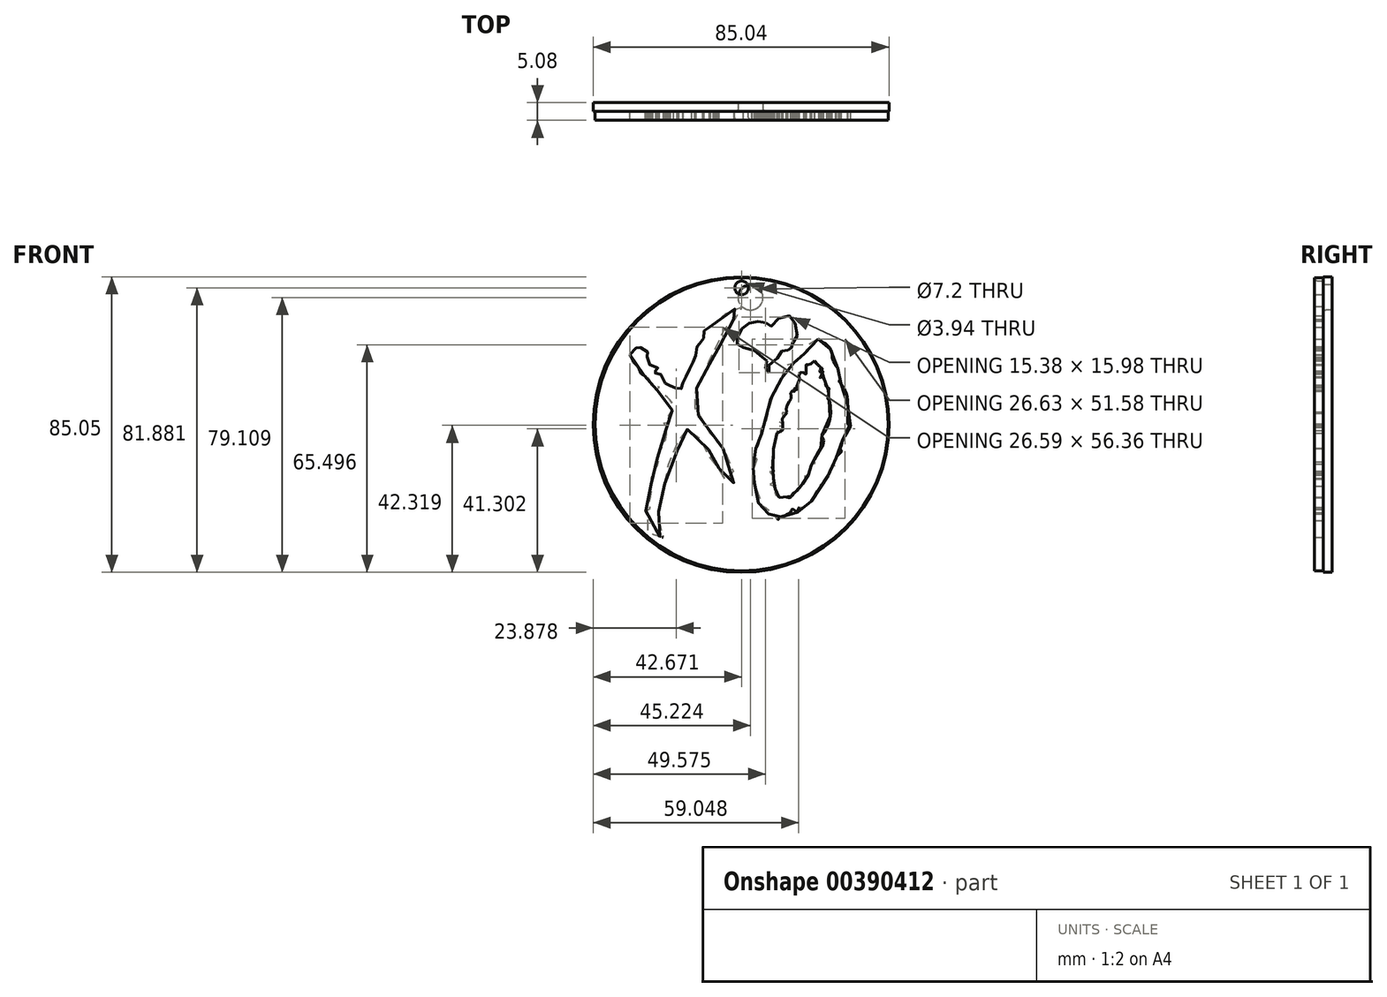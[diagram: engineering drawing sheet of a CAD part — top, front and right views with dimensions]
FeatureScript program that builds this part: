
annotation { "Feature Type Name" : "Feature", "Feature Type Description" : "" }
export const myFeature = defineFeature(function(context is Context, id is Id, definition is map)
    precondition{}
    {
        {
            var Q0;
            Q0=qCreatedBy(makeId("Front.planeOp"),FACE);
            var sketch = newSketch(context, id + "F0", { "sketchPlane" : qUnion([Q0])});
            skFitSpline(sketch, "E0", {"points": [v(-32.07, 22.35) * mm, v(-30.03, 24.5) * mm, v(-29.2, 24.47) * mm, v(-26.86, 22.8) * mm, v(-27.16, 21.56) * mm, v(-25.57, 18.73) * mm, v(-23.72, 18.35) * mm, v(-25.5, 17.07) * mm, v(-23.46, 16.95) * mm, v(-23.16, 16.39) * mm, v(-21, 13.14) * mm, v(-20.44, 13.6) * mm, v(-17.68, 12.08) * mm, v(-17.23, 13.4) * mm, v(-16.47, 14.84) * mm, v(-15.34, 17.37) * mm, v(-14.1, 19.94) * mm, v(-13.11, 22.28) * mm, v(-12.66, 25.26) * mm, v(-12.28, 25.49) * mm, v(-10.96, 26.85) * mm, v(-10.7, 29.22) * mm, v(-9.26, 30.17) * mm], "startDerivative": vector(41.67, 50.3) * mm, "endDerivative": vector(43.04, 15.46) * mm});
            skPoint(sketch, "E1.6.internal.orphan", {"position": v(0, 36.12) * mm});
            skPoint(sketch, "E1.9.internal.orphan", {"position": v(0, 34.47) * mm});
            skFitSpline(sketch, "E2", {"points": [v(-9.26, 30.17) * mm, v(-6.77, 32.25) * mm, v(-5.19, 33.64) * mm, v(-3.26, 34.93) * mm, v(-1.52, 35.68) * mm, v(0, 36.12) * mm, v(0.48, 34.44) * mm, v(0, 34.06) * mm, v(-1.49, 32.55) * mm, v(-2.66, 32.4) * mm, v(-2.92, 31.04) * mm, v(-4.35, 30.17) * mm, v(-6.05, 27) * mm, v(-6.62, 24.32) * mm, v(-7.6, 24.32) * mm, v(-7.19, 23.15) * mm, v(-8.5, 22.54) * mm, v(-9.26, 19.94) * mm, v(-9.87, 17.86) * mm, v(-11.04, 17.1) * mm, v(-11.04, 15.57) * mm, v(-12.24, 13.35) * mm, v(-13.4, 11.72) * mm, v(-13.13, 10.44) * mm, v(-14.17, 9.99) * mm, v(-13.37, 6.87) * mm, v(-11, 2.31) * mm, v(-8.06, -1.39) * mm, v(-5.72, -4.26) * mm, v(-4.51, -6.1) * mm, v(-3.11, -8.68) * mm, v(-2.36, -11.32) * mm, v(-2.62, -15.43) * mm, v(-4.51, -13.85) * mm, v(-5.04, -12.94) * mm, v(-6.78, -11.24) * mm, v(-6.4, -10.49) * mm, v(-7.98, -9.28) * mm, v(-8.1, -7.5) * mm, v(-9.26, -7.17) * mm, v(-8.85, -6.49) * mm, v(-9.9, -4.3) * mm, v(-11.91, -1.88) * mm, v(-14.06, 0.39) * mm, v(-15.16, 1.33) * mm, v(-16.03, 0.39) * mm, v(-16.82, 0) * mm, v(-16.74, -1.05) * mm, v(-18.48, -3.09) * mm, v(-18.03, -4.3) * mm, v(-21.05, -9.4) * mm, v(-20.67, -11.07) * mm, v(-22.49, -13.85) * mm, v(-21.95, -15.13) * mm, v(-23.98, -19.56) * mm, v(-23.72, -21.1) * mm, v(-24.36, -21.53) * mm, v(-23.72, -23.08) * mm, v(-23.98, -24.95) * mm, v(-24.25, -28.7) * mm, v(-22.44, -30.19) * mm, v(-25.59, -29.33) * mm, v(-27.03, -27.46) * mm, v(-26.81, -24.85) * mm, v(-27.67, -22.7) * mm, v(-26.17, -21.75) * mm, v(-26.65, -20.63) * mm, v(-25.7, -17.1) * mm, v(-26.01, -15.4) * mm, v(-25.9, -13.15) * mm, v(-25.1, -11.07) * mm, v(-23.61, -8.19) * mm, v(-24.25, -7.92) * mm, v(-23.88, -6.74) * mm, v(-22.8, -3.97) * mm, v(-21.85, -2.15) * mm, v(-21.58, 0) * mm, v(-21.98, 2.16) * mm, v(-22.25, 2.75) * mm, v(-20.54, 3.15) * mm, v(-20.9, 4.5) * mm, v(-20.23, 5.8) * mm, v(-19.6, 7.73) * mm, v(-20.32, 8.85) * mm, v(-21.75, 10.38) * mm, v(-23.55, 11.28) * mm, v(-24.22, 12.54) * mm, v(-23.55, 12.94) * mm, v(-25.8, 13.43) * mm, v(-26.07, 14.33) * mm, v(-27.19, 15.77) * mm, v(-29.07, 17.12) * mm, v(-29.53, 18.44) * mm, v(-30.59, 19.68) * mm, v(-31.42, 20.9) * mm, v(-32.07, 22.35) * mm], "startDerivative": vector(198.2, 161.84) * mm, "endDerivative": vector(-64.93, 159.65) * mm});
            skFitSpline(sketch, "E3", {"points": [v(7.84, 17.17) * mm, v(8.1, 17.59) * mm, v(7.87, 18.73) * mm, v(8.41, 20.32) * mm, v(10.64, 21.56) * mm, v(10.76, 22.28) * mm, v(11.9, 23.62) * mm, v(12.92, 23.75) * mm, v(13.3, 23.52) * mm, v(13.24, 24.29) * mm, v(13.78, 24.5) * mm, v(14.48, 24.35) * mm, v(14.2, 24.76) * mm, v(14.2, 25.24) * mm, v(15.08, 25.81) * mm, v(15.87, 27.27) * mm, v(15.97, 29.18) * mm, v(15.12, 32.2) * mm, v(14.3, 33.38) * mm, v(12.32, 33.2) * mm, v(10.61, 32.64) * mm, v(10.2, 31.8) * mm, v(7.78, 30.17) * mm, v(7.56, 30.73) * mm, v(6.37, 31.83) * mm, v(5.45, 31.97) * mm, v(4.01, 31.76) * mm, v(2.73, 31.5) * mm, v(1.6, 31.1) * mm, v(0.42, 30.17) * mm, v(-0.46, 28.64) * mm, v(-1.42, 26.87) * mm, v(-1.96, 25.7) * mm, v(-1.04, 25.28) * mm, v(-0.26, 24.24) * mm, v(0.84, 24.45) * mm, v(3.07, 23.86) * mm, v(5.16, 22.35) * mm, v(6.13, 21.4) * mm, v(6.45, 20.87) * mm, v(6.84, 21.1) * mm, v(7.54, 19.36) * mm, v(7.2, 19.06) * mm, v(6.81, 17.86) * mm, v(7.25, 17.11) * mm, v(7.84, 17.17) * mm]});
            skFitSpline(sketch, "E4", {"points": [v(20.97, 20.5) * mm, v(19.16, 19.4) * mm, v(18.55, 19.52) * mm, v(18.59, 16.76) * mm, v(17.76, 17.21) * mm, v(16.63, 16.87) * mm, v(16.59, 14.84) * mm, v(15.87, 13.25) * mm, v(15.83, 12.2) * mm, v(15.04, 12.83) * mm, v(15.42, 11.93) * mm, v(14.47, 11.82) * mm, v(14.1, 11.21) * mm, v(14.25, 10.04) * mm, v(13.95, 9.13) * mm, v(12.85, 7.06) * mm, v(12.93, 5.85) * mm], "startDerivative": vector(-24.49, -22.05) * mm, "endDerivative": vector(4.9, -18.32) * mm});
            skFitSpline(sketch, "E5", {"points": [v(13.12, 5.65) * mm, v(12.63, 5.43) * mm, v(12.2, 5.79) * mm, v(11.64, 5.5) * mm, v(11.8, 4.67) * mm, v(11.76, 4.01) * mm, v(11.35, 3.66) * mm, v(10.63, 3.54) * mm, v(10.68, 3.18) * mm, v(11.08, 2.94) * mm, v(11.58, 2.62) * mm, v(11.87, 2.26) * mm, v(11.91, 1.8) * mm, v(11.58, 1.59) * mm, v(10.92, 1.75) * mm, v(11.49, 1.19) * mm, v(11.82, 0.62) * mm, v(11.55, 0.44) * mm, v(11.35, 0) * mm, v(10.92, -0.25) * mm, v(10.63, 0.4) * mm, v(10.23, 0.49) * mm, v(10.16, -0.61) * mm, v(10, -1.39) * mm, v(9.82, -2.63) * mm, v(9.38, -4.02) * mm, v(8.9, -6.2) * mm, v(8.67, -8.45) * mm, v(8.73, -9.97) * mm, v(9.18, -11.6) * mm, v(8.06, -11.24) * mm, v(8.76, -12.23) * mm, v(9.18, -13.4) * mm, v(8.73, -14.7) * mm, v(8.16, -15.12) * mm, v(8.95, -15.3) * mm, v(9.46, -16.04) * mm, v(10.26, -16.93) * mm, v(9.75, -17.15) * mm, v(9.62, -17.6) * mm, v(10.32, -18.39) * mm, v(10.92, -18.8) * mm, v(11.65, -18.83) * mm, v(12.54, -18.74) * mm, v(13.24, -18.74) * mm, v(14.03, -18.74) * mm, v(14.72, -17.77) * mm, v(15.87, -16.89) * mm, v(16.72, -15.9) * mm, v(17.58, -14.83) * mm, v(18.11, -13.8) * mm, v(18.38, -12.75) * mm, v(18.27, -11.9) * mm, v(19.18, -12.38) * mm, v(19.53, -12.06) * mm, v(19.6, -11.47) * mm, v(19.85, -10.72) * mm, v(20.09, -10.16) * mm, v(20.17, -9.47) * mm, v(19.93, -8.7) * mm, v(19.85, -8.56) * mm, v(20.57, -8.83) * mm, v(21.13, -9.1) * mm, v(21.02, -8) * mm, v(21.1, -7.33) * mm, v(21.53, -6.66) * mm, v(21.8, -6.16) * mm, v(22.1, -5.7) * mm, v(22.73, -4.8) * mm, v(23.52, -3.5) * mm, v(23.63, -2.25) * mm, v(23.14, -1.39) * mm, v(23.1, -0.78) * mm, v(23.93, 0) * mm, v(25.21, 3) * mm, v(25.44, 4.24) * mm, v(25.67, 6.1) * mm, v(25.52, 7.8) * mm, v(25.37, 8.77) * mm, v(24.99, 9.57) * mm, v(24.54, 10.06) * mm, v(24.99, 10.44) * mm, v(25.06, 11.04) * mm, v(24.99, 11.9) * mm, v(24.87, 12.21) * mm, v(25.18, 12.55) * mm, v(24.61, 12.89) * mm, v(24.2, 13.95) * mm, v(23.93, 14.84) * mm, v(23.52, 15.76) * mm, v(23.18, 16.02) * mm, v(22.65, 15.68) * mm, v(22.6, 16.1) * mm, v(23.02, 16.44) * mm, v(23.33, 16.95) * mm, v(23.35, 17.61) * mm, v(22.85, 17.5) * mm, v(22.45, 17.3) * mm, v(22.26, 17.72) * mm, v(23, 18.12) * mm, v(23.4, 18.41) * mm, v(22.74, 18.73) * mm, v(22.02, 19.32) * mm, v(21.62, 19.67) * mm, v(20.97, 20.5) * mm], "startDerivative": vector(-68, -52.97) * mm, "endDerivative": vector(-62.66, 87.14) * mm});
            skFitSpline(sketch, "E6", {"points": [v(22.02, 26.76) * mm, v(21.26, 26.2) * mm, v(19.4, 25.29) * mm, v(18.27, 24.2) * mm, v(17.93, 23.51) * mm, v(18.08, 22.28) * mm, v(17.7, 22.28) * mm, v(16.88, 21.56) * mm, v(16.35, 21.56) * mm, v(15.86, 21.56) * mm, v(15.63, 20.5) * mm, v(14.46, 19.66) * mm, v(13.63, 19.32) * mm, v(12.6, 19.32) * mm, v(12.38, 18.41) * mm, v(11.67, 15.89) * mm, v(10.65, 13.6) * mm, v(9.82, 12.55) * mm, v(8.87, 10.9) * mm, v(8.5, 10.19) * mm, v(8.68, 8.41) * mm, v(8.81, 7.64) * mm, v(7.58, 6.01) * mm, v(7.02, 5.32) * mm, v(7.05, 4.3) * mm, v(7.08, 2.92) * mm, v(6.12, 2.33) * mm, v(5.66, 1.77) * mm, v(5.56, 0.7) * mm, v(5.74, -0.37) * mm, v(5.2, -1.39) * mm, v(4.91, -1.94) * mm, v(4.67, -3.36) * mm, v(4.78, -4.7) * mm, v(4.27, -4.56) * mm, v(3.9, -4.88) * mm, v(3.69, -5.5) * mm, v(4.25, -6.08) * mm, v(4.4, -7.3) * mm, v(3.72, -9.65) * mm, v(3.09, -10.73) * mm, v(3.79, -12.64) * mm, v(2.96, -13.46) * mm, v(4.1, -13.27) * mm, v(3.66, -14.8) * mm, v(4.23, -16.39) * mm, v(4.23, -18.1) * mm, v(5.12, -18.74) * mm, v(4.74, -19.94) * mm, v(5.5, -20.96) * mm, v(6.2, -21.47) * mm, v(6.26, -22.3) * mm, v(6.9, -21.66) * mm, v(7.52, -23.4) * mm, v(8.74, -23.43) * mm, v(9.36, -23.83) * mm, v(9.36, -24.96) * mm, v(10.08, -25.36) * mm, v(10.92, -24.64) * mm, v(12.22, -24.07) * mm, v(13.42, -23.49) * mm, v(14.03, -23.14) * mm, v(14.78, -22.13) * mm, v(16.03, -23.09) * mm, v(16.49, -21.83) * mm, v(17.15, -21.6) * mm, v(18.36, -21.22) * mm, v(19.42, -20.58) * mm, v(19.85, -20.26) * mm, v(20.97, -17.97) * mm, v(22.73, -15.18) * mm, v(24.64, -13.4) * mm, v(25.18, -11.24) * mm, v(26.48, -9.65) * mm, v(27.3, -9.46) * mm, v(27.11, -8.38) * mm, v(27.18, -7.3) * mm, v(27.94, -6.35) * mm, v(28.7, -5.7) * mm, v(28.38, -5.02) * mm, v(28.7, -3.78) * mm, v(29.08, -2.32) * mm, v(29.62, -1.39) * mm, v(30.26, -0.25) * mm, v(30.8, 0.62) * mm, v(31.24, 1.58) * mm, v(31.24, 2.35) * mm, v(30.58, 2.06) * mm, v(30.51, 2.47) * mm, v(30.51, 3.68) * mm, v(30.6, 7.15) * mm, v(30.52, 8.09) * mm, v(30.52, 9.26) * mm, v(30.38, 10.33) * mm, v(30.07, 11.23) * mm, v(28.9, 13.6) * mm, v(28.09, 14.55) * mm, v(28.02, 14.84) * mm, v(28.36, 15.4) * mm, v(28.29, 16.3) * mm, v(28.13, 17.14) * mm, v(27.84, 17.94) * mm, v(27.32, 19) * mm, v(26.09, 21.14) * mm, v(26.02, 22.09) * mm, v(26.02, 22.8) * mm, v(25.57, 23.84) * mm, v(25.18, 24.51) * mm, v(24.7, 24.98) * mm, v(24.25, 25.43) * mm, v(23.7, 25.75) * mm, v(23.1, 26.15) * mm, v(22.02, 26.76) * mm]});
            skCircle(sketch, "E7", {"center": v(0.02, 2.28) * mm, "radius": 42.13 * mm});
            skCircle(sketch, "E8", {"center": v(0.02, 41.55) * mm, "radius": 1.97 * mm});
            skLineSegment(sketch, "E9", {"start": v(12.93, 5.85) * mm, "end": v(13.12, 5.65) * mm});
            skSolve(sketch);
        }
        {
            var Q0;
            Q0 = qSketchRegion(id + "F0", true);
            extrude(context, id + "F1", {"entities" : qUnion([Q0]), "depth" : 2.54 * mm});
        }
        {
            var Q0;
            Q0=makeQuery(id+"F0.imprint","IMPRINT",FACE,{"disambiguationData":[TD([[makeQuery(id+"F0.imprint","IMPRINT",EDGE,{"derivedFrom":sQuery(id+"F0.wireOp",EDGE,"E4")}),1.0]])]});
            extrude(context, id + "F2", {"entities" : qUnion([Q0]), "depth" : 2.54 * mm});
        }
        {
            var Q0;
            Q0=qCreatedBy(makeId("Front.planeOp"),FACE);
            var sketch = newSketch(context, id + "F3", { "sketchPlane" : qUnion([Q0])});
            skCircle(sketch, "E10", {"center": v(-0.13, 2.2) * mm, "radius": 42.52 * mm});
            skPoint(sketch, "E10.first.point", {"position": v(-42.6, 0) * mm});
            skPoint(sketch, "E10.second.point", {"position": v(42.3, 4.9) * mm});
            skPoint(sketch, "E10.third.point", {"position": v(2.88, 44.6) * mm});
            skCircle(sketch, "E11", {"center": v(2.57, 38.78) * mm, "radius": 3.6 * mm});
            skPoint(sketch, "E11.first.point", {"position": v(0, 41.3) * mm});
            skPoint(sketch, "E11.second.point", {"position": v(5.15, 36.26) * mm});
            skPoint(sketch, "E11.third.point", {"position": v(0, 36.26) * mm});
            skSolve(sketch);
        }
        {
            var Q0;
            Q0 = qSketchRegion(id + "F3", true);
            extrude(context, id + "F4", {"entities" : qUnion([Q0]), "oppositeDirection" : true, "depth" : 2.54 * mm});
        }
        {
            var Q0;
            Q0=makeQuery(id+"F1.opExtrude","CAP_EDGE",EDGE,{"disambiguationData":[OSD([sQuery(id+"F0.wireOp",EDGE,"E8")])],"isStart":false});
            fillet(context, id + "F5", {"entities" : qUnion([Q0]), "radius" : 0.76 * mm, "tangentPropagation" : true, "allowEdgeOverflow" : false});
        }
        {
            var Q0;
            Q0=makeQuery(id+"F4.opExtrude","CAP_EDGE",EDGE,{"disambiguationData":[OSD([sQuery(id+"F3.wireOp",EDGE,"E11")])],"isStart":true});
            fillet(context, id + "F6", {"entities" : qUnion([Q0]), "radius" : 0.76 * mm, "tangentPropagation" : true, "allowEdgeOverflow" : false});
        }
    });
